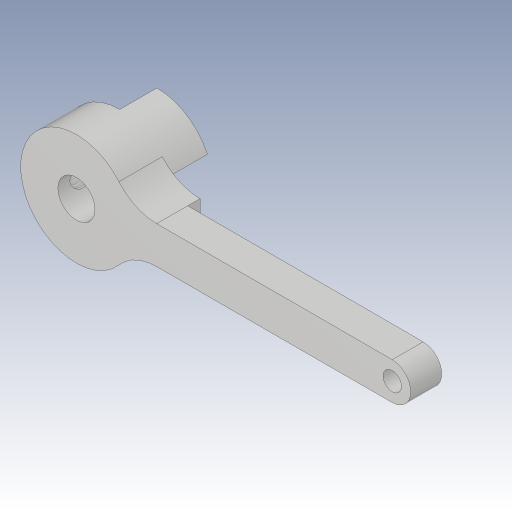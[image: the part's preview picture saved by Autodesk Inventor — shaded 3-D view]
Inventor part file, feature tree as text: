
AUTODESK INVENTOR PART (.ipt)
format: ipt  version: 2023.3 (Build 273359000, 359)  size: 194,048 bytes
history: native  units: in
note: dims shown in document units (in); Inventor stores cm internally (conversion verified against a paired STEP export)
features: sketch x4, extrude x3, fillet x2, hole x2, projected_geometry x2, plane x1
ambient origin geometry x8: Origin, YZ Plane, XZ Plane, XY Plane, X Axis, Y Axis, Z Axis, Center Point
bodies: Body1 (feature_tree)
feature tree (14):
  sketch  "Skizze3"  dims[d4=0.1181in d5=0.3543in d6=0.1181in]
  extrude  "Extrusion3"  Depth=0.1181in
  fillet  "Rundung1"  Radius=0.1181in
  plane  "Arbeitsebene1"
  hole  "Bohrung1"  [1 undecoded]
  extrude  "Extrusion4"  Depth=0.1181in TaperAngle=0.0deg
  hole  "Bohrung2"  [1 undecoded]
  fillet  "Rundung2"  Radius=0.0591in
  extrude  "Extrusion5"  Depth=0.0591in
  sketch  "Skizze4"  dims[d7=1.063in d8=0.1378in d9=0.0in]
  sketch  "Skizze5"  dims[d10=0.1575in]
  projected_geometry  "Projizierte Kontur1"
  sketch  "Skizze6"  dims[d11=0.0617in d12=0.1772in d13=0.2559in d14=0.0945in d15=90.0deg d16=0.1772in d17=0.0in d22=0.1181in d23=0.0in d24=0.1718in d25=0.0591in d26=0.0591in d27=0.1772in d28=0.1575in d29=0.0787in d30=90.0deg d31=0.1772in d32=0.0in d33=0.0591in d34=0.0394in d35=0.0in]
  projected_geometry  "Projizierte Kontur2"
note: 2 required parameter values undecoded (feature->parameter linkage not recoverable at this tier; creation-order binding heuristic only, values carry confidence <= 0.55)
